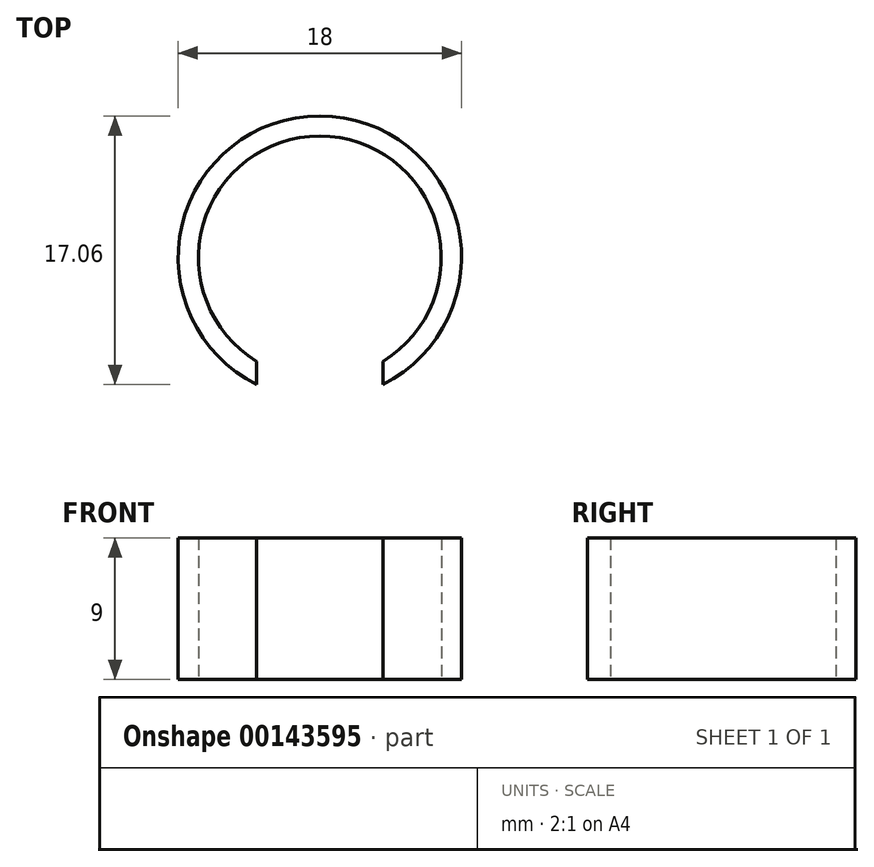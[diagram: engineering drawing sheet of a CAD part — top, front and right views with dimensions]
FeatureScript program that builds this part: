
annotation { "Feature Type Name" : "Feature", "Feature Type Description" : "" }
export const myFeature = defineFeature(function(context is Context, id is Id, definition is map)
    precondition{}
    {
        {
            var Q0;
            Q0=qCreatedBy(makeId("Top.planeOp"),FACE);
            var sketch = newSketch(context, id + "F0", { "sketchPlane" : qUnion([Q0])});
            skCircle(sketch, "E0", {"center": v(0, 0) * mm, "radius": 9 * mm});
            skCircle(sketch, "E1", {"center": v(0, 0) * mm, "radius": 7.71 * mm});
            skLineSegment(sketch, "E2", {"start": v(4.01, -6.59) * mm, "end": v(4.01, -8.06) * mm});
            skLineSegment(sketch, "E3", {"start": v(0, 9) * mm, "end": v(0, -9) * mm});
            skLineSegment(sketch, "E4.MirrorCS", {"start": v(-4.01, -6.59) * mm, "end": v(-4.01, -8.06) * mm});
            skSolve(sketch);
        }
        {
            var Q0;
            {var subQ3=sQuery(id+"F0.wireOp",EDGE,"E4.MirrorCS");Q0=makeQuery(id+"F0.imprint","IMPRINT",FACE,{"disambiguationData":[TD([[makeQuery(id+"F0.imprint","IMPRINT",EDGE,{"derivedFrom":subQ3}),-1.0]])]});}
            var Q1;
            {var subQ0=sQuery(id+"F0.wireOp",EDGE,"E2");Q1=makeQuery(id+"F0.imprint","IMPRINT",FACE,{"disambiguationData":[TD([[makeQuery(id+"F0.imprint","IMPRINT",EDGE,{"derivedFrom":subQ0}),1.0]])]});}
            extrude(context, id + "F1", {"entities" : qUnion([Q0, Q1]), "depth" : 9 * mm});
        }
    });
